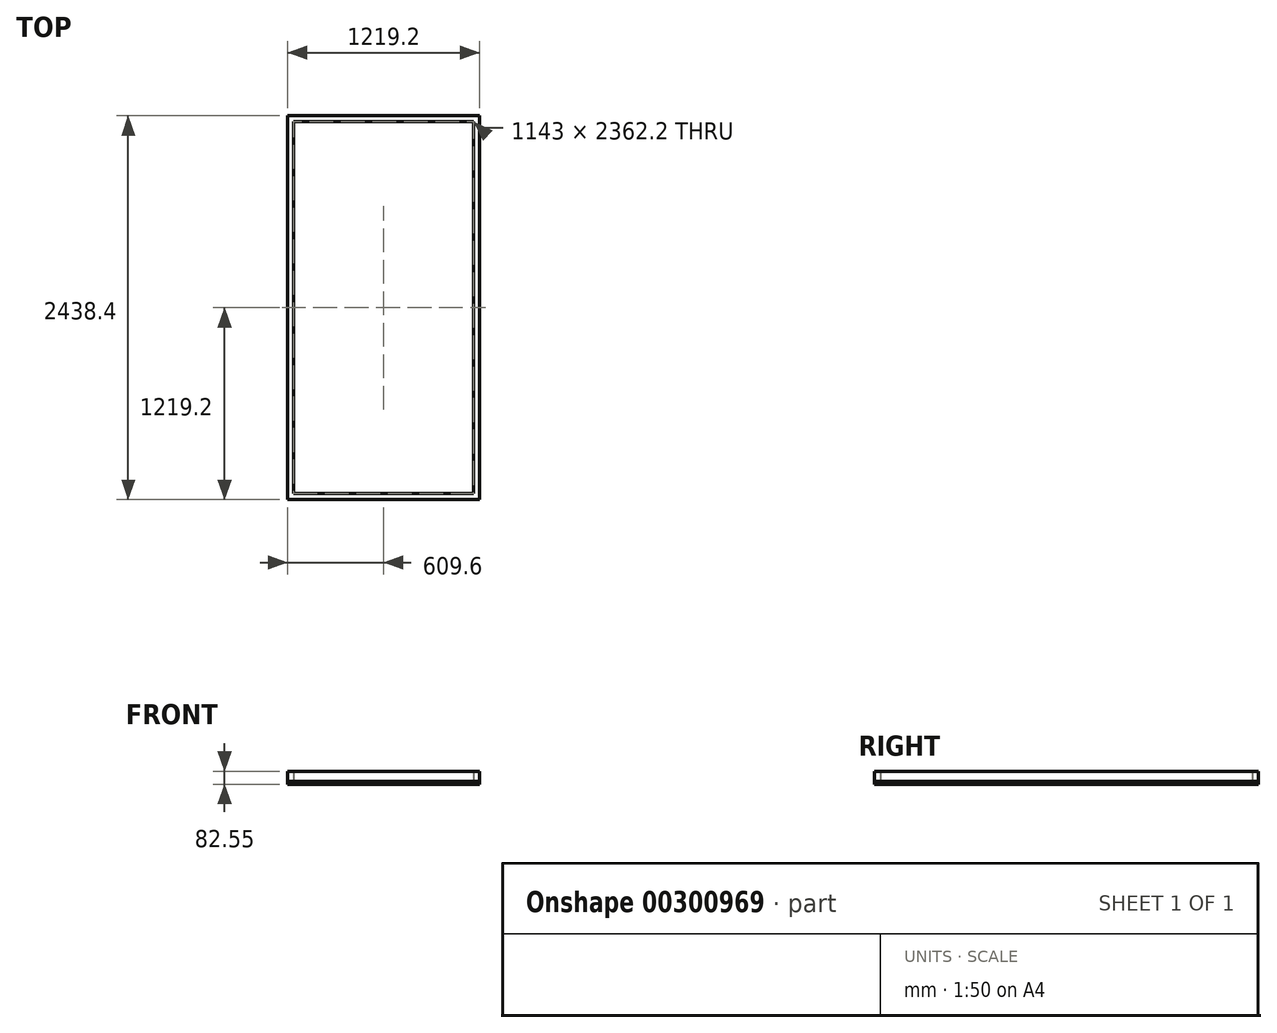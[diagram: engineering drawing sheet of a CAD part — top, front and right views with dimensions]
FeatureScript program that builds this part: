
annotation { "Feature Type Name" : "Feature", "Feature Type Description" : "" }
export const myFeature = defineFeature(function(context is Context, id is Id, definition is map)
    precondition{}
    {
        {
            var Q0;
            Q0=qCreatedBy(makeId("Top.planeOp"),FACE);
            var sketch = newSketch(context, id + "F0", { "sketchPlane" : qUnion([Q0])});
            skLineSegment(sketch, "E0.bottom", {"start": v(609.6, -1219.2) * mm, "end": v(-609.6, -1219.2) * mm});
            skLineSegment(sketch, "E0.top", {"start": v(609.6, 1219.2) * mm, "end": v(-609.6, 1219.2) * mm});
            skLineSegment(sketch, "E0.left", {"start": v(609.6, -1219.2) * mm, "end": v(609.6, 1219.2) * mm});
            skLineSegment(sketch, "E0.right", {"start": v(-609.6, -1219.2) * mm, "end": v(-609.6, 1219.2) * mm});
            skPoint(sketch, "E0.middle", {"position": v(0, 0) * mm});
            skSolve(sketch);
        }
        {
            var Q0;
            Q0=qSketchRegion(id+"F0",true);
            extrude(context, id + "F1", {"entities" : qUnion([Q0]), "oppositeDirection" : true, "depth" : 19.05 * mm});
        }
        {
            var Q0;
            Q0=makeQuery(id+"F1.opExtrude","CAP_FACE",FACE,{"disambiguationData":[OSD([sQuery(id+"F0.wireOp",EDGE,"E0.bottom"),sQuery(id+"F0.wireOp",EDGE,"E0.top"),sQuery(id+"F0.wireOp",EDGE,"E0.left"),sQuery(id+"F0.wireOp",EDGE,"E0.right")])],"isStart":true});
            var sketch = newSketch(context, id + "F2", { "sketchPlane" : qUnion([Q0])});
            skLineSegment(sketch, "E1.bottom", {"start": v(-609.6, 1219.2) * mm, "end": v(609.6, 1219.2) * mm});
            skLineSegment(sketch, "E1.top", {"start": v(-609.6, 1181.1) * mm, "end": v(609.6, 1181.1) * mm});
            skLineSegment(sketch, "E1.left", {"start": v(-609.6, 1219.2) * mm, "end": v(-609.6, 1181.1) * mm});
            skLineSegment(sketch, "E1.right", {"start": v(609.6, 1219.2) * mm, "end": v(609.6, 1181.1) * mm});
            skLineSegment(sketch, "E2.bottom", {"start": v(-609.6, -1219.2) * mm, "end": v(609.6, -1219.2) * mm});
            skLineSegment(sketch, "E2.top", {"start": v(-609.6, -1181.1) * mm, "end": v(609.6, -1181.1) * mm});
            skLineSegment(sketch, "E2.left", {"start": v(-609.6, -1219.2) * mm, "end": v(-609.6, -1181.1) * mm});
            skLineSegment(sketch, "E2.right", {"start": v(609.6, -1219.2) * mm, "end": v(609.6, -1181.1) * mm});
            skLineSegment(sketch, "E3.bottom", {"start": v(-609.6, 1181.1) * mm, "end": v(-571.5, 1181.1) * mm});
            skLineSegment(sketch, "E3.top", {"start": v(-609.6, -1181.1) * mm, "end": v(-571.5, -1181.1) * mm});
            skLineSegment(sketch, "E3.left", {"start": v(-609.6, 1181.1) * mm, "end": v(-609.6, -1181.1) * mm});
            skLineSegment(sketch, "E3.right", {"start": v(-571.5, 1181.1) * mm, "end": v(-571.5, -1181.1) * mm});
            skLineSegment(sketch, "E4.bottom", {"start": v(609.6, 1181.1) * mm, "end": v(571.5, 1181.1) * mm});
            skLineSegment(sketch, "E4.top", {"start": v(609.6, -1181.1) * mm, "end": v(571.5, -1181.1) * mm});
            skLineSegment(sketch, "E4.left", {"start": v(609.6, 1181.1) * mm, "end": v(609.6, -1181.1) * mm});
            skLineSegment(sketch, "E4.right", {"start": v(571.5, 1181.1) * mm, "end": v(571.5, -1181.1) * mm});
            skSolve(sketch);
        }
        {
            var Q0;
            Q0=qSketchRegion(id+"F2",true);
            extrude(context, id + "F3", {"entities" : qUnion([Q0]), "depth" : 63.5 * mm});
        }
    });
